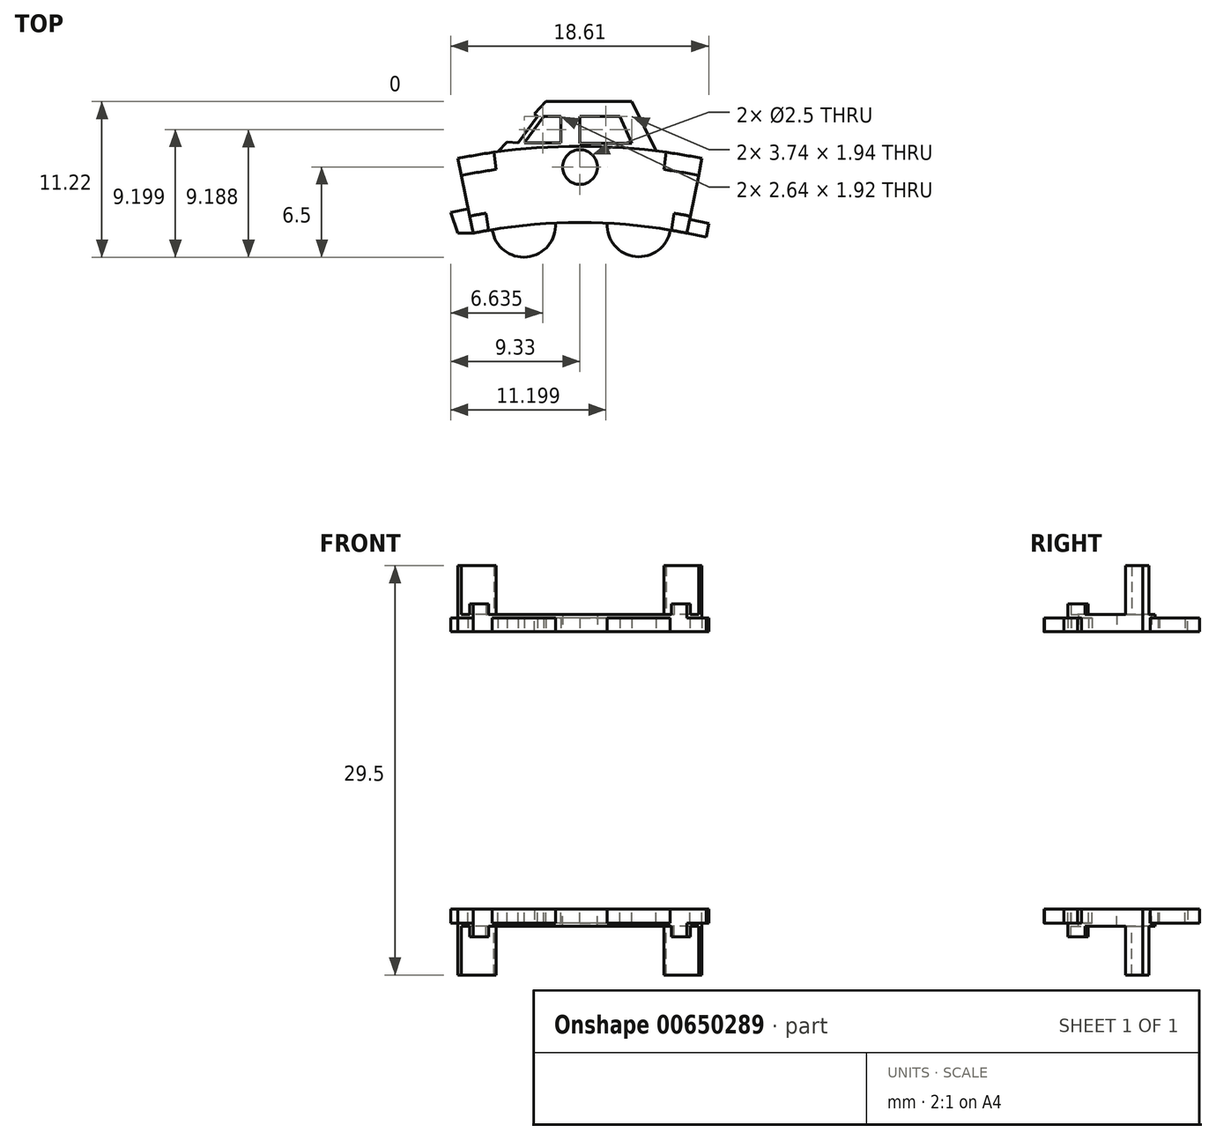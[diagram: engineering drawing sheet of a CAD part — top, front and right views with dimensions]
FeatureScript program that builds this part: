
annotation { "Feature Type Name" : "Feature", "Feature Type Description" : "" }
export const myFeature = defineFeature(function(context is Context, id is Id, definition is map)
    precondition{}
    {
        {
            var Q0;
            Q0=qCreatedBy(makeId("Top.planeOp"),FACE);
            var sketch = newSketch(context, id + "F0", { "sketchPlane" : qUnion([Q0])});
            skCircle(sketch, "E0", {"center": v(0, 0) * mm, "radius": 39 * mm});
            skCircle(sketch, "E1", {"center": v(0, 0) * mm, "radius": 44.5 * mm});
            skCircle(sketch, "E2", {"center": v(0, 43) * mm, "radius": 1.25 * mm});
            skCircle(sketch, "E3", {"center": v(0, 43) * mm, "radius": 6 * mm});
            skLineSegment(sketch, "E4", {"start": v(-7.7, 38.23) * mm, "end": v(-8.8, 43.62) * mm});
            skLineSegment(sketch, "E5", {"start": v(7.7, 38.23) * mm, "end": v(8.8, 43.62) * mm});
            skLineSegment(sketch, "E6", {"start": v(-7.5, 43.86) * mm, "end": v(-6.58, 38.44) * mm});
            skLineSegment(sketch, "E7", {"start": v(6.58, 38.44) * mm, "end": v(7.5, 43.86) * mm});
            skCircle(sketch, "E8", {"center": v(0, 0) * mm, "radius": 40.25 * mm});
            skCircle(sketch, "E9", {"center": v(0, 0) * mm, "radius": 43.25 * mm});
            skSolve(sketch);
        }
        {
            var Q0;
            {var subQ0=sQuery(id+"F0.wireOp",EDGE,"E7");var subQ1=sQuery(id+"F0.wireOp",EDGE,"E1");var subQ2=makeQuery(id+"F0.imprint","INTERSECT",VERTEX,{"derivedFrom":[subQ1,subQ0]});Q0=makeQuery(id+"F0.imprint","IMPRINT",FACE,{"disambiguationData":[TD([[makeQuery(id+"F0.imprint","IMPRINT",EDGE,{"disambiguationData":[TD([[subQ2,-1.0]])],"derivedFrom":subQ1}),1.0]])]});}
            var Q1;
            {var subQ0=sQuery(id+"F0.wireOp",EDGE,"E6");var subQ1=sQuery(id+"F0.wireOp",EDGE,"E1");var subQ2=makeQuery(id+"F0.imprint","INTERSECT",VERTEX,{"derivedFrom":[subQ1,subQ0]});Q1=makeQuery(id+"F0.imprint","IMPRINT",FACE,{"disambiguationData":[TD([[makeQuery(id+"F0.imprint","IMPRINT",EDGE,{"disambiguationData":[TD([[subQ2,1.0]])],"derivedFrom":subQ1}),1.0]])]});}
            var Q2;
            {var subQ0=sQuery(id+"F0.wireOp",EDGE,"E3");var subQ1=sQuery(id+"F0.wireOp",EDGE,"E1");var subQ2=makeQuery(id+"F0.imprint","INTERSECT",VERTEX,{"disambiguationData":[OD(0.0)],"derivedFrom":[subQ1,subQ0]});Q2=makeQuery(id+"F0.imprint","IMPRINT",FACE,{"disambiguationData":[TD([[makeQuery(id+"F0.imprint","IMPRINT",EDGE,{"disambiguationData":[TD([[subQ2,-1.0]])],"derivedFrom":subQ1}),1.0]])]});}
            var Q3;
            {var subQ0=sQuery(id+"F0.wireOp",EDGE,"E8");var subQ1=sQuery(id+"F0.wireOp",EDGE,"E3");var subQ2=makeQuery(id+"F0.imprint","INTERSECT",VERTEX,{"disambiguationData":[OD(1.0)],"derivedFrom":[subQ1,subQ0]});Q3=makeQuery(id+"F0.imprint","IMPRINT",FACE,{"disambiguationData":[TD([[makeQuery(id+"F0.imprint","IMPRINT",EDGE,{"disambiguationData":[TD([[subQ2,-1.0]])],"derivedFrom":subQ1}),-1.0]])]});}
            var Q4;
            {var subQ3=sQuery(id+"F0.wireOp",EDGE,"E9");var subQ5=sQuery(id+"F0.wireOp",EDGE,"E2");var subQ6=makeQuery(id+"F0.imprint","INTERSECT",VERTEX,{"disambiguationData":[OD(0.0)],"derivedFrom":[subQ5,subQ3]});Q4=makeQuery(id+"F0.imprint","IMPRINT",FACE,{"disambiguationData":[TD([[makeQuery(id+"F0.imprint","IMPRINT",EDGE,{"disambiguationData":[TD([[subQ6,1.0]])],"derivedFrom":subQ5}),-1.0]])]});}
            var Q5;
            {var subQ0=sQuery(id+"F0.wireOp",EDGE,"E9");var subQ1=sQuery(id+"F0.wireOp",EDGE,"E3");var subQ2=makeQuery(id+"F0.imprint","INTERSECT",VERTEX,{"disambiguationData":[OD(0.0)],"derivedFrom":[subQ1,subQ0]});Q5=makeQuery(id+"F0.imprint","IMPRINT",FACE,{"disambiguationData":[TD([[makeQuery(id+"F0.imprint","IMPRINT",EDGE,{"disambiguationData":[TD([[subQ2,-1.0]])],"derivedFrom":subQ1}),-1.0]])]});}
            var Q6;
            {var subQ0=sQuery(id+"F0.wireOp",EDGE,"E6");var subQ1=sQuery(id+"F0.wireOp",EDGE,"E0");var subQ2=makeQuery(id+"F0.imprint","INTERSECT",VERTEX,{"derivedFrom":[subQ1,subQ0]});Q6=makeQuery(id+"F0.imprint","IMPRINT",FACE,{"disambiguationData":[TD([[makeQuery(id+"F0.imprint","IMPRINT",EDGE,{"disambiguationData":[TD([[subQ2,1.0]])],"derivedFrom":subQ1}),-1.0]])]});}
            var Q7;
            {var subQ0=sQuery(id+"F0.wireOp",EDGE,"E3");var subQ1=sQuery(id+"F0.wireOp",EDGE,"E0");var subQ2=makeQuery(id+"F0.imprint","INTERSECT",VERTEX,{"disambiguationData":[OD(0.0)],"derivedFrom":[subQ1,subQ0]});Q7=makeQuery(id+"F0.imprint","IMPRINT",FACE,{"disambiguationData":[TD([[makeQuery(id+"F0.imprint","IMPRINT",EDGE,{"disambiguationData":[TD([[subQ2,-1.0]])],"derivedFrom":subQ1}),-1.0]])]});}
            var Q8;
            {var subQ0=sQuery(id+"F0.wireOp",EDGE,"E7");var subQ1=sQuery(id+"F0.wireOp",EDGE,"E0");var subQ2=makeQuery(id+"F0.imprint","INTERSECT",VERTEX,{"derivedFrom":[subQ1,subQ0]});Q8=makeQuery(id+"F0.imprint","IMPRINT",FACE,{"disambiguationData":[TD([[makeQuery(id+"F0.imprint","IMPRINT",EDGE,{"disambiguationData":[TD([[subQ2,-1.0]])],"derivedFrom":subQ1}),-1.0]])]});}
            var Q9;
            {var subQ0=sQuery(id+"F0.wireOp",EDGE,"E8");var subQ1=sQuery(id+"F0.wireOp",EDGE,"E5");var subQ2=makeQuery(id+"F0.imprint","INTERSECT",VERTEX,{"derivedFrom":[subQ1,subQ0]});Q9=makeQuery(id+"F0.imprint","IMPRINT",FACE,{"disambiguationData":[TD([[makeQuery(id+"F0.imprint","IMPRINT",EDGE,{"disambiguationData":[TD([[subQ2,-1.0]])],"derivedFrom":subQ1}),1.0]])]});}
            var Q10;
            {var subQ0=sQuery(id+"F0.wireOp",EDGE,"E8");var subQ1=sQuery(id+"F0.wireOp",EDGE,"E4");var subQ2=makeQuery(id+"F0.imprint","INTERSECT",VERTEX,{"derivedFrom":[subQ1,subQ0]});Q10=makeQuery(id+"F0.imprint","IMPRINT",FACE,{"disambiguationData":[TD([[makeQuery(id+"F0.imprint","IMPRINT",EDGE,{"disambiguationData":[TD([[subQ2,-1.0]])],"derivedFrom":subQ1}),-1.0]])]});}
            extrude(context, id + "F1", {"entities" : qUnion([Q0, Q1, Q2, Q3, Q4, Q5, Q6, Q7, Q8, Q9, Q10]), "depth" : 1.25 * mm, "offsetDistance" : 25 * mm});
        }
        {
            var Q0;
            Q0=qCreatedBy(makeId("Top.planeOp"),FACE);
            var sketch = newSketch(context, id + "F2", { "sketchPlane" : qUnion([Q0])});
            skCircle(sketch, "E10", {"center": v(0, 0) * mm, "radius": 39 * mm});
            skCircle(sketch, "E11", {"center": v(0, 0) * mm, "radius": 44.5 * mm});
            skCircle(sketch, "E12", {"center": v(0, 43) * mm, "radius": 0.85 * mm});
            skCircle(sketch, "E13", {"center": v(0, 43) * mm, "radius": 6 * mm});
            skLineSegment(sketch, "E14", {"start": v(-7.7, 38.23) * mm, "end": v(-8.8, 43.62) * mm});
            skLineSegment(sketch, "E15", {"start": v(7.7, 38.23) * mm, "end": v(8.8, 43.62) * mm});
            skLineSegment(sketch, "E16", {"start": v(-6.2, 44.06) * mm, "end": v(-5.44, 38.62) * mm});
            skLineSegment(sketch, "E17", {"start": v(5.44, 38.62) * mm, "end": v(6.2, 44.06) * mm});
            skCircle(sketch, "E18", {"center": v(0, 0) * mm, "radius": 40.25 * mm});
            skCircle(sketch, "E19", {"center": v(0, 0) * mm, "radius": 43.25 * mm});
            skSolve(sketch);
        }
        {
            var Q0;
            {var subQ0=sQuery(id+"F2.wireOp",EDGE,"E15");var subQ1=sQuery(id+"F2.wireOp",EDGE,"E11");var subQ2=makeQuery(id+"F2.imprint","INTERSECT",VERTEX,{"derivedFrom":[subQ1,subQ0]});Q0=makeQuery(id+"F2.imprint","IMPRINT",FACE,{"disambiguationData":[TD([[makeQuery(id+"F2.imprint","IMPRINT",EDGE,{"disambiguationData":[TD([[subQ2,-1.0]])],"derivedFrom":subQ1}),1.0]])]});}
            var Q1;
            {var subQ0=sQuery(id+"F2.wireOp",EDGE,"E14");var subQ1=sQuery(id+"F2.wireOp",EDGE,"E11");var subQ2=makeQuery(id+"F2.imprint","INTERSECT",VERTEX,{"derivedFrom":[subQ1,subQ0]});Q1=makeQuery(id+"F2.imprint","IMPRINT",FACE,{"disambiguationData":[TD([[makeQuery(id+"F2.imprint","IMPRINT",EDGE,{"disambiguationData":[TD([[subQ2,1.0]])],"derivedFrom":subQ1}),1.0]])]});}
            extrude(context, id + "F3", {"entities" : qUnion([Q0, Q1]), "operationType" : NewBodyOperationType.ADD, "depth" : 4.75 * mm, "offsetDistance" : 25 * mm});
        }
        {
            var Q0;
            Q0=qCreatedBy(makeId("Top.planeOp"),FACE);
            var sketch = newSketch(context, id + "F4", { "sketchPlane" : qUnion([Q0])});
            skCircle(sketch, "E20", {"center": v(0, 0) * mm, "radius": 39 * mm});
            skCircle(sketch, "E21", {"center": v(0, 0) * mm, "radius": 44.5 * mm});
            skCircle(sketch, "E22", {"center": v(0, 43) * mm, "radius": 0.85 * mm});
            skCircle(sketch, "E23", {"center": v(0, 43) * mm, "radius": 6 * mm});
            skLineSegment(sketch, "E24", {"start": v(-7.7, 38.23) * mm, "end": v(-8.8, 43.62) * mm});
            skLineSegment(sketch, "E25", {"start": v(7.7, 38.23) * mm, "end": v(8.8, 43.62) * mm});
            skLineSegment(sketch, "E26", {"start": v(-7.5, 43.86) * mm, "end": v(-6.58, 38.44) * mm});
            skLineSegment(sketch, "E27", {"start": v(6.58, 38.44) * mm, "end": v(7.5, 43.86) * mm});
            skCircle(sketch, "E28", {"center": v(0, 0) * mm, "radius": 40.25 * mm});
            skCircle(sketch, "E29", {"center": v(0, 0) * mm, "radius": 43.25 * mm});
            skSolve(sketch);
        }
        {
            var Q0;
            {var subQ0=sQuery(id+"F4.wireOp",EDGE,"E24");var subQ1=sQuery(id+"F4.wireOp",EDGE,"E20");var subQ2=makeQuery(id+"F4.imprint","INTERSECT",VERTEX,{"derivedFrom":[subQ1,subQ0]});Q0=makeQuery(id+"F4.imprint","IMPRINT",FACE,{"disambiguationData":[TD([[makeQuery(id+"F4.imprint","IMPRINT",EDGE,{"disambiguationData":[TD([[subQ2,1.0]])],"derivedFrom":subQ1}),-1.0]])]});}
            var Q1;
            {var subQ0=sQuery(id+"F4.wireOp",EDGE,"E25");var subQ1=sQuery(id+"F4.wireOp",EDGE,"E20");var subQ2=makeQuery(id+"F4.imprint","INTERSECT",VERTEX,{"derivedFrom":[subQ1,subQ0]});Q1=makeQuery(id+"F4.imprint","IMPRINT",FACE,{"disambiguationData":[TD([[makeQuery(id+"F4.imprint","IMPRINT",EDGE,{"disambiguationData":[TD([[subQ2,-1.0]])],"derivedFrom":subQ1}),-1.0]])]});}
            extrude(context, id + "F5", {"entities" : qUnion([Q0, Q1]), "operationType" : NewBodyOperationType.ADD, "depth" : 2 * mm, "offsetDistance" : 25 * mm});
        }
        {
            var Q0;
            {var subQ0=sQuery(id+"F4.wireOp",EDGE,"E28");var subQ1=sQuery(id+"F4.wireOp",EDGE,"E20");var subQ2=sQuery(id+"F2.wireOp",EDGE,"E19");var subQ3=sQuery(id+"F2.wireOp",EDGE,"E11");Q0=makeQuery(id+"F5.boolean.opBoolean","MERGE",FACE,{"derivedFrom":[makeQuery(id+"F3.boolean.opBoolean","MERGE",FACE,{"derivedFrom":[makeQuery(id+"F1.opExtrude","CAP_FACE",FACE,{"disambiguationData":[OSD([sQuery(id+"F0.wireOp",EDGE,"E0"),sQuery(id+"F0.wireOp",EDGE,"E1"),sQuery(id+"F0.wireOp",EDGE,"E2"),sQuery(id+"F0.wireOp",EDGE,"E4"),sQuery(id+"F0.wireOp",EDGE,"E5"),sQuery(id+"F0.wireOp",EDGE,"E6"),sQuery(id+"F0.wireOp",EDGE,"E7"),sQuery(id+"F0.wireOp",EDGE,"E8"),sQuery(id+"F0.wireOp",EDGE,"E9")])],"isStart":true}),makeQuery(id+"F3.opExtrude","CAP_FACE",FACE,{"disambiguationData":[OSD([subQ3,sQuery(id+"F2.wireOp",EDGE,"E15"),sQuery(id+"F2.wireOp",EDGE,"E17"),subQ2])],"isStart":true}),makeQuery(id+"F3.opExtrude","CAP_FACE",FACE,{"disambiguationData":[OSD([subQ3,sQuery(id+"F2.wireOp",EDGE,"E14"),sQuery(id+"F2.wireOp",EDGE,"E16"),subQ2])],"isStart":true})]}),makeQuery(id+"F5.opExtrude","CAP_FACE",FACE,{"disambiguationData":[OSD([subQ1,sQuery(id+"F4.wireOp",EDGE,"E25"),sQuery(id+"F4.wireOp",EDGE,"E27"),subQ0])],"isStart":true}),makeQuery(id+"F5.opExtrude","CAP_FACE",FACE,{"disambiguationData":[OSD([subQ1,sQuery(id+"F4.wireOp",EDGE,"E24"),sQuery(id+"F4.wireOp",EDGE,"E26"),subQ0])],"isStart":true})]});}
            var sketch = newSketch(context, id + "F6", { "sketchPlane" : qUnion([Q0])});
            skLineSegment(sketch, "E30", {"start": v(5.46, -44.16) * mm, "end": v(3.74, -47.72) * mm});
            skLineSegment(sketch, "E31", {"start": v(3.74, -47.72) * mm, "end": v(-2.45, -47.72) * mm});
            skLineSegment(sketch, "E32", {"start": v(-2.45, -47.72) * mm, "end": v(-5.92, -44.1) * mm});
            skLineSegment(sketch, "E33", {"start": v(-5.92, -44.1) * mm, "end": v(5.46, -44.16) * mm});
            skSolve(sketch);
        }
        {
            var Q0;
            {var subQ0=sQuery(id+"F6.wireOp",EDGE,"E30");Q0=makeQuery(id+"F6.imprint","IMPRINT",FACE,{"disambiguationData":[TD([[makeQuery(id+"F6.imprint","IMPRINT",EDGE,{"derivedFrom":subQ0}),-1.0]])]});}
            extrude(context, id + "F7", {"entities" : qUnion([Q0]), "operationType" : NewBodyOperationType.ADD, "oppositeDirection" : true, "depth" : 1 * mm, "offsetDistance" : 25 * mm});
        }
        {
            var Q0;
            {var subQ0=sQuery(id+"F2.wireOp",EDGE,"E11");var subQ1=sQuery(id+"F0.wireOp",EDGE,"E1");var subQ2=sQuery(id+"F4.wireOp",EDGE,"E28");var subQ3=sQuery(id+"F4.wireOp",EDGE,"E20");var subQ4=sQuery(id+"F2.wireOp",EDGE,"E19");Q0=makeQuery(id+"F7.boolean.opBoolean","MERGE",FACE,{"derivedFrom":[makeQuery(id+"F5.boolean.opBoolean","MERGE",FACE,{"derivedFrom":[makeQuery(id+"F3.boolean.opBoolean","MERGE",FACE,{"derivedFrom":[makeQuery(id+"F1.opExtrude","CAP_FACE",FACE,{"disambiguationData":[OSD([sQuery(id+"F0.wireOp",EDGE,"E0"),subQ1,sQuery(id+"F0.wireOp",EDGE,"E2"),sQuery(id+"F0.wireOp",EDGE,"E4"),sQuery(id+"F0.wireOp",EDGE,"E5"),sQuery(id+"F0.wireOp",EDGE,"E6"),sQuery(id+"F0.wireOp",EDGE,"E7"),sQuery(id+"F0.wireOp",EDGE,"E8"),sQuery(id+"F0.wireOp",EDGE,"E9")])],"isStart":true}),makeQuery(id+"F3.opExtrude","CAP_FACE",FACE,{"disambiguationData":[OSD([subQ0,sQuery(id+"F2.wireOp",EDGE,"E15"),sQuery(id+"F2.wireOp",EDGE,"E17"),subQ4])],"isStart":true}),makeQuery(id+"F3.opExtrude","CAP_FACE",FACE,{"disambiguationData":[OSD([subQ0,sQuery(id+"F2.wireOp",EDGE,"E14"),sQuery(id+"F2.wireOp",EDGE,"E16"),subQ4])],"isStart":true})]}),makeQuery(id+"F5.opExtrude","CAP_FACE",FACE,{"disambiguationData":[OSD([subQ3,sQuery(id+"F4.wireOp",EDGE,"E25"),sQuery(id+"F4.wireOp",EDGE,"E27"),subQ2])],"isStart":true}),makeQuery(id+"F5.opExtrude","CAP_FACE",FACE,{"disambiguationData":[OSD([subQ3,sQuery(id+"F4.wireOp",EDGE,"E24"),sQuery(id+"F4.wireOp",EDGE,"E26"),subQ2])],"isStart":true})]}),makeQuery(id+"F7.opExtrude","CAP_FACE",FACE,{"disambiguationData":[OSD([subQ1,subQ0,sQuery(id+"F6.wireOp",EDGE,"E30"),sQuery(id+"F6.wireOp",EDGE,"E31"),sQuery(id+"F6.wireOp",EDGE,"E32")])],"isStart":true})]});}
            var sketch = newSketch(context, id + "F8", { "sketchPlane" : qUnion([Q0])});
            skLineSegment(sketch, "E34", {"start": v(2.87, -46.66) * mm, "end": v(0, -46.66) * mm});
            skLineSegment(sketch, "E35", {"start": v(0, -46.66) * mm, "end": v(0, -44.72) * mm});
            skLineSegment(sketch, "E36", {"start": v(0, -44.72) * mm, "end": v(3.74, -44.72) * mm});
            skLineSegment(sketch, "E37", {"start": v(3.74, -44.72) * mm, "end": v(2.87, -46.66) * mm});
            skLineSegment(sketch, "E38", {"start": v(-1.38, -46.66) * mm, "end": v(-1.38, -44.74) * mm});
            skLineSegment(sketch, "E39", {"start": v(-1.38, -44.74) * mm, "end": v(-4.01, -44.74) * mm});
            skLineSegment(sketch, "E40", {"start": v(-4.01, -44.74) * mm, "end": v(-2.62, -46.66) * mm});
            skLineSegment(sketch, "E41", {"start": v(-2.62, -46.66) * mm, "end": v(-1.38, -46.66) * mm});
            skLineSegment(sketch, "E42", {"start": v(-5.92, -48.92) * mm, "end": v(-3.06, -46.66) * mm});
            skLineSegment(sketch, "E43", {"start": v(-3.06, -46.66) * mm, "end": v(-4.45, -44.74) * mm});
            skLineSegment(sketch, "E44", {"start": v(-4.45, -44.74) * mm, "end": v(-5.5, -44.84) * mm});
            skLineSegment(sketch, "E45", {"start": v(-5.5, -44.84) * mm, "end": v(-5.92, -48.92) * mm});
            skSolve(sketch);
        }
        {
            var Q0;
            Q0 = qSketchRegion(id + "F8", true);
            extrude(context, id + "F9", {"entities" : qUnion([Q0]), "operationType" : NewBodyOperationType.REMOVE, "oppositeDirection" : true, "depth" : 25 * mm, "offsetDistance" : 25 * mm});
        }
        {
            var Q0;
            {var subQ0=sQuery(id+"F2.wireOp",EDGE,"E11");var subQ1=sQuery(id+"F0.wireOp",EDGE,"E1");var subQ2=sQuery(id+"F4.wireOp",EDGE,"E28");var subQ3=sQuery(id+"F4.wireOp",EDGE,"E20");var subQ4=sQuery(id+"F2.wireOp",EDGE,"E19");Q0=makeQuery(id+"F7.boolean.opBoolean","MERGE",FACE,{"derivedFrom":[makeQuery(id+"F5.boolean.opBoolean","MERGE",FACE,{"derivedFrom":[makeQuery(id+"F3.boolean.opBoolean","MERGE",FACE,{"derivedFrom":[makeQuery(id+"F1.opExtrude","CAP_FACE",FACE,{"disambiguationData":[OSD([sQuery(id+"F0.wireOp",EDGE,"E0"),subQ1,sQuery(id+"F0.wireOp",EDGE,"E2"),sQuery(id+"F0.wireOp",EDGE,"E4"),sQuery(id+"F0.wireOp",EDGE,"E5"),sQuery(id+"F0.wireOp",EDGE,"E6"),sQuery(id+"F0.wireOp",EDGE,"E7"),sQuery(id+"F0.wireOp",EDGE,"E8"),sQuery(id+"F0.wireOp",EDGE,"E9")])],"isStart":true}),makeQuery(id+"F3.opExtrude","CAP_FACE",FACE,{"disambiguationData":[OSD([subQ0,sQuery(id+"F2.wireOp",EDGE,"E15"),sQuery(id+"F2.wireOp",EDGE,"E17"),subQ4])],"isStart":true}),makeQuery(id+"F3.opExtrude","CAP_FACE",FACE,{"disambiguationData":[OSD([subQ0,sQuery(id+"F2.wireOp",EDGE,"E14"),sQuery(id+"F2.wireOp",EDGE,"E16"),subQ4])],"isStart":true})]}),makeQuery(id+"F5.opExtrude","CAP_FACE",FACE,{"disambiguationData":[OSD([subQ3,sQuery(id+"F4.wireOp",EDGE,"E25"),sQuery(id+"F4.wireOp",EDGE,"E27"),subQ2])],"isStart":true}),makeQuery(id+"F5.opExtrude","CAP_FACE",FACE,{"disambiguationData":[OSD([subQ3,sQuery(id+"F4.wireOp",EDGE,"E24"),sQuery(id+"F4.wireOp",EDGE,"E26"),subQ2])],"isStart":true})]}),makeQuery(id+"F7.opExtrude","CAP_FACE",FACE,{"disambiguationData":[OSD([subQ1,subQ0,sQuery(id+"F6.wireOp",EDGE,"E30"),sQuery(id+"F6.wireOp",EDGE,"E31"),sQuery(id+"F6.wireOp",EDGE,"E32")])],"isStart":true})]});}
            var sketch = newSketch(context, id + "F10", { "sketchPlane" : qUnion([Q0])});
            skCircle(sketch, "E46", {"center": v(-4.05, -38.79) * mm, "radius": 2.29 * mm});
            skCircle(sketch, "E47", {"center": v(4.24, -38.82) * mm, "radius": 2.29 * mm});
            skSolve(sketch);
        }
        {
            var Q0;
            Q0 = qSketchRegion(id + "F10", true);
            var Q1;
            {var subQ0=sQuery(id+"F10.wireOp",EDGE,"E46");var subQ1=sQuery(id+"F4.wireOp",EDGE,"E20");var subQ2=makeQuery(id+"F5.boolean.opBoolean","MERGE",EDGE,{"derivedFrom":[makeQuery(id+"F1.opExtrude","CAP_EDGE",EDGE,{"disambiguationData":[OSD([sQuery(id+"F0.wireOp",EDGE,"E0")])],"isStart":true}),makeQuery(id+"F5.opExtrude","CAP_EDGE",EDGE,{"disambiguationData":[OSD([subQ1]),TDD([makeQuery(id+"F4.imprint","IMPRINT",EDGE,{"disambiguationData":[TD([[makeQuery(id+"F4.imprint","INTERSECT",VERTEX,{"derivedFrom":[subQ1,sQuery(id+"F4.wireOp",EDGE,"E25")]}),-1.0]])],"derivedFrom":subQ1})])],"isStart":true}),makeQuery(id+"F5.opExtrude","CAP_EDGE",EDGE,{"disambiguationData":[OSD([subQ1]),TDD([makeQuery(id+"F4.imprint","IMPRINT",EDGE,{"disambiguationData":[TD([[makeQuery(id+"F4.imprint","INTERSECT",VERTEX,{"derivedFrom":[subQ1,sQuery(id+"F4.wireOp",EDGE,"E24")]}),1.0]])],"derivedFrom":subQ1})])],"isStart":true})]});var subQ3=makeQuery(id+"F10.imprint","INTERSECT",VERTEX,{"disambiguationData":[OD(0.0)],"derivedFrom":[subQ2,subQ0]});Q1=makeQuery(id+"F10.imprint","IMPRINT",FACE,{"disambiguationData":[TD([[makeQuery(id+"F10.imprint","IMPRINT",EDGE,{"disambiguationData":[TD([[subQ3,1.0]])],"derivedFrom":subQ0}),1.0]])]});}
            extrude(context, id + "F11", {"entities" : qUnion([Q0, Q1]), "operationType" : NewBodyOperationType.ADD, "oppositeDirection" : true, "depth" : 1 * mm, "offsetDistance" : 25 * mm});
        }
        {
            var Q0;
            {var subQ0=sQuery(id+"F4.wireOp",EDGE,"E20");var subQ1=sQuery(id+"F0.wireOp",EDGE,"E0");var subQ2=sQuery(id+"F2.wireOp",EDGE,"E11");var subQ3=sQuery(id+"F0.wireOp",EDGE,"E1");var subQ4=sQuery(id+"F4.wireOp",EDGE,"E28");var subQ5=sQuery(id+"F2.wireOp",EDGE,"E19");Q0=makeQuery(id+"F11.boolean.opBoolean","MERGE",FACE,{"derivedFrom":[makeQuery(id+"F7.boolean.opBoolean","MERGE",FACE,{"derivedFrom":[makeQuery(id+"F5.boolean.opBoolean","MERGE",FACE,{"derivedFrom":[makeQuery(id+"F3.boolean.opBoolean","MERGE",FACE,{"derivedFrom":[makeQuery(id+"F1.opExtrude","CAP_FACE",FACE,{"disambiguationData":[OSD([subQ1,subQ3,sQuery(id+"F0.wireOp",EDGE,"E2"),sQuery(id+"F0.wireOp",EDGE,"E4"),sQuery(id+"F0.wireOp",EDGE,"E5"),sQuery(id+"F0.wireOp",EDGE,"E6"),sQuery(id+"F0.wireOp",EDGE,"E7"),sQuery(id+"F0.wireOp",EDGE,"E8"),sQuery(id+"F0.wireOp",EDGE,"E9")])],"isStart":true}),makeQuery(id+"F3.opExtrude","CAP_FACE",FACE,{"disambiguationData":[OSD([subQ2,sQuery(id+"F2.wireOp",EDGE,"E15"),sQuery(id+"F2.wireOp",EDGE,"E17"),subQ5])],"isStart":true}),makeQuery(id+"F3.opExtrude","CAP_FACE",FACE,{"disambiguationData":[OSD([subQ2,sQuery(id+"F2.wireOp",EDGE,"E14"),sQuery(id+"F2.wireOp",EDGE,"E16"),subQ5])],"isStart":true})]}),makeQuery(id+"F5.opExtrude","CAP_FACE",FACE,{"disambiguationData":[OSD([subQ0,sQuery(id+"F4.wireOp",EDGE,"E25"),sQuery(id+"F4.wireOp",EDGE,"E27"),subQ4])],"isStart":true}),makeQuery(id+"F5.opExtrude","CAP_FACE",FACE,{"disambiguationData":[OSD([subQ0,sQuery(id+"F4.wireOp",EDGE,"E24"),sQuery(id+"F4.wireOp",EDGE,"E26"),subQ4])],"isStart":true})]}),makeQuery(id+"F7.opExtrude","CAP_FACE",FACE,{"disambiguationData":[OSD([subQ3,subQ2,sQuery(id+"F6.wireOp",EDGE,"E30"),sQuery(id+"F6.wireOp",EDGE,"E31"),sQuery(id+"F6.wireOp",EDGE,"E32")])],"isStart":true})]}),makeQuery(id+"F11.opExtrude","CAP_FACE",FACE,{"disambiguationData":[OSD([subQ1,subQ0,sQuery(id+"F10.wireOp",EDGE,"E46"),sQuery(id+"F10.wireOp",EDGE,"E46")])],"isStart":true}),makeQuery(id+"F11.opExtrude","CAP_FACE",FACE,{"disambiguationData":[OSD([sQuery(id+"F10.wireOp",EDGE,"E47")])],"isStart":true})]});}
            var sketch = newSketch(context, id + "F12", { "sketchPlane" : qUnion([Q0])});
            skLineSegment(sketch, "E48", {"start": v(-8.06, -39.98) * mm, "end": v(-9.33, -39.72) * mm});
            skLineSegment(sketch, "E49", {"start": v(-9.33, -39.72) * mm, "end": v(-8.8, -38.23) * mm});
            skLineSegment(sketch, "E50", {"start": v(-8.8, -38.23) * mm, "end": v(-7.7, -38.23) * mm});
            skLineSegment(sketch, "E51", {"start": v(-7.7, -38.23) * mm, "end": v(-8.06, -39.98) * mm});
            skLineSegment(sketch, "E52", {"start": v(8.06, -39.98) * mm, "end": v(7.7, -38.23) * mm});
            skLineSegment(sketch, "E53", {"start": v(7.7, -38.23) * mm, "end": v(9.08, -37.95) * mm});
            skLineSegment(sketch, "E54", {"start": v(9.08, -37.95) * mm, "end": v(9.28, -38.93) * mm});
            skLineSegment(sketch, "E55", {"start": v(9.28, -38.93) * mm, "end": v(7.9, -39.21) * mm});
            skLineSegment(sketch, "E56", {"start": v(7.9, -39.21) * mm, "end": v(7.7, -38.23) * mm});
            skSolve(sketch);
        }
        {
            var Q0;
            Q0 = qSketchRegion(id + "F12", true);
            extrude(context, id + "F13", {"entities" : qUnion([Q0]), "operationType" : NewBodyOperationType.ADD, "oppositeDirection" : true, "depth" : 1 * mm, "offsetDistance" : 25 * mm});
        }
        {
            var Q0;
            Q0=makeQuery(id+"F1.opExtrude","SWEPT_BODY",BODY,{"disambiguationData":[OSD([sQuery(id+"F0.wireOp",EDGE,"E0"),sQuery(id+"F0.wireOp",EDGE,"E1"),sQuery(id+"F0.wireOp",EDGE,"E2"),sQuery(id+"F0.wireOp",EDGE,"E4"),sQuery(id+"F0.wireOp",EDGE,"E5"),sQuery(id+"F0.wireOp",EDGE,"E6"),sQuery(id+"F0.wireOp",EDGE,"E7"),sQuery(id+"F0.wireOp",EDGE,"E8"),sQuery(id+"F0.wireOp",EDGE,"E9")])]});
            transform(context, id + "F14", {"entities" : qUnion([Q0]), "transformType" : TransformType.TRANSLATION_3D, "dx" : 0 * mm, "dy" : 0 * mm, "dz" : 10 * mm, "makeCopy" : false});
        }
        {
            var Q0;
            Q0=makeQuery(id+"F1.opExtrude","SWEPT_BODY",BODY,{"disambiguationData":[OSD([sQuery(id+"F0.wireOp",EDGE,"E0"),sQuery(id+"F0.wireOp",EDGE,"E1"),sQuery(id+"F0.wireOp",EDGE,"E2"),sQuery(id+"F0.wireOp",EDGE,"E4"),sQuery(id+"F0.wireOp",EDGE,"E5"),sQuery(id+"F0.wireOp",EDGE,"E6"),sQuery(id+"F0.wireOp",EDGE,"E7"),sQuery(id+"F0.wireOp",EDGE,"E8"),sQuery(id+"F0.wireOp",EDGE,"E9")])]});
            var Q1;
            Q1=qCreatedBy(makeId("Top.planeOp"),FACE);
            mirror(context, id + "F15", {"entities" : qUnion([Q0]), "mirrorPlane" : qUnion([Q1])});
        }
    });
